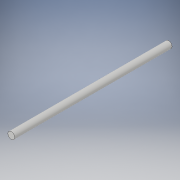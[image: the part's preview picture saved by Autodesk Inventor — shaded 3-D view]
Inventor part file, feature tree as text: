
AUTODESK INVENTOR PART (.ipt)
format: ipt  version: 2019 (Build 230136000, 136)  size: 90,112 bytes
history: native  units: mm
features: extrude x1, sketch x1
ambient origin geometry x8: Origin, YZ Plane, XZ Plane, XY Plane, X Axis, Y Axis, Z Axis, Center Point
bodies: Solid1 (feature_tree)
feature tree (2):
  extrude  "Extrusion1"  Depth=69.0mm TaperAngle=0.0deg
  sketch  "Sketch1"  dims[d0=3.0mm d1=69.0mm d2=0.0mm]
